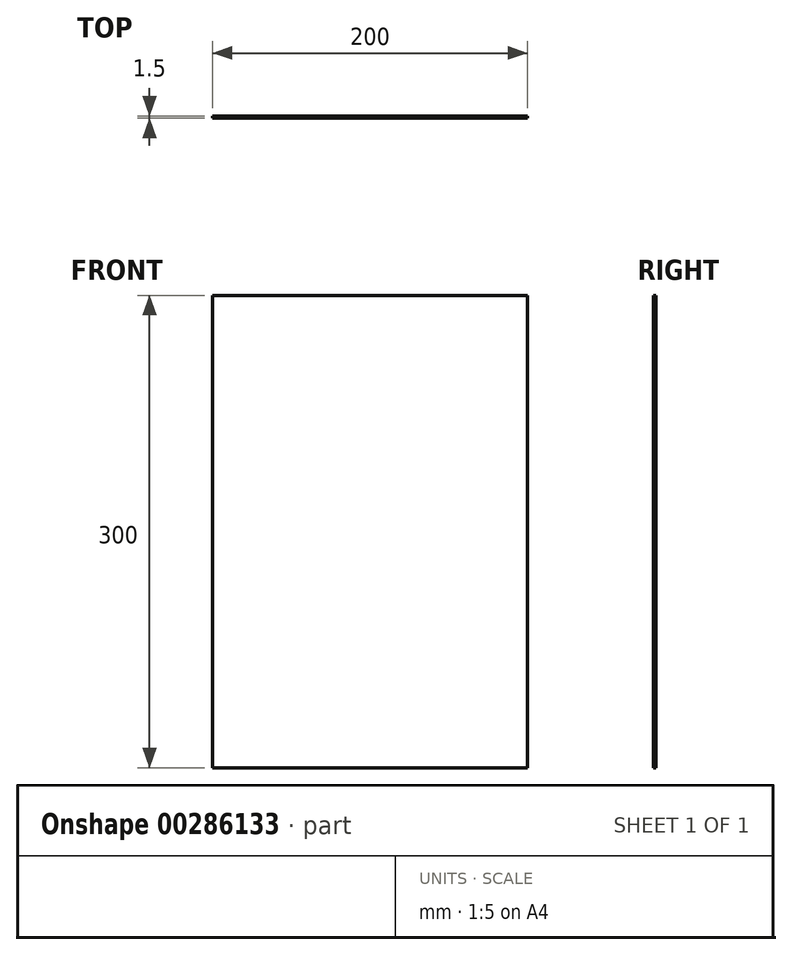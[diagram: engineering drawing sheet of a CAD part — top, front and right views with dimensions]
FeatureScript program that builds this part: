
annotation { "Feature Type Name" : "Feature", "Feature Type Description" : "" }
export const myFeature = defineFeature(function(context is Context, id is Id, definition is map)
    precondition{}
    {
        {
            var Q0;
            Q0=qCreatedBy(makeId("Front.planeOp"),FACE);
            var sketch = newSketch(context, id + "F0", { "sketchPlane" : qUnion([Q0])});
            skLineSegment(sketch, "E0.bottom", {"start": v(0, 0) * mm, "end": v(200, 0) * mm});
            skLineSegment(sketch, "E0.top", {"start": v(0, 300) * mm, "end": v(200, 300) * mm});
            skLineSegment(sketch, "E0.left", {"start": v(0, 0) * mm, "end": v(0, 300) * mm});
            skLineSegment(sketch, "E0.right", {"start": v(200, 0) * mm, "end": v(200, 300) * mm});
            skSolve(sketch);
        }
        {
            var Q0;
            Q0 = qSketchRegion(id + "F0", true);
            extrude(context, id + "F1", {"entities" : qUnion([Q0]), "depth" : 1.5 * mm});
        }
    });
